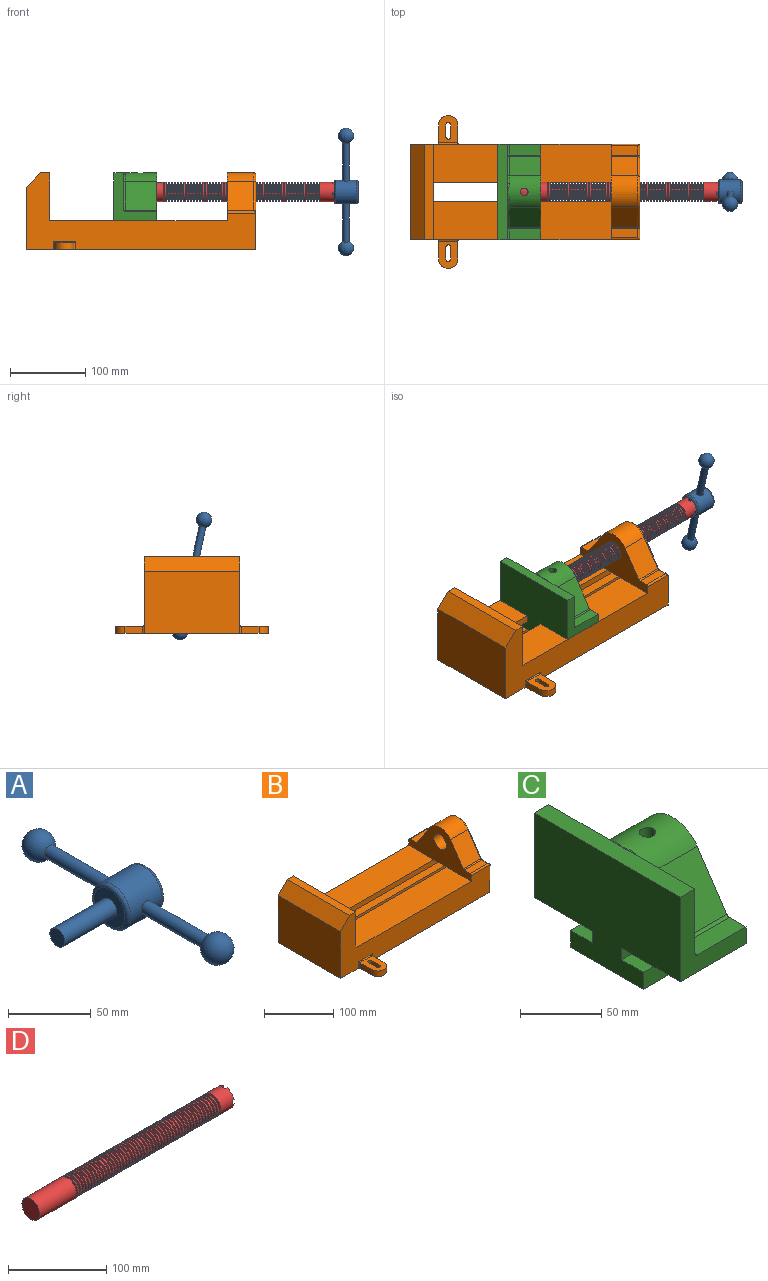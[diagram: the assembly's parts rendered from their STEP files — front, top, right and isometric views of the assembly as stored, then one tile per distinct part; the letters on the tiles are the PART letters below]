
ASSEMBLY  parts=4 mates=4
PART A: 11 faces, bbox 76.2x172.7x34.4 mm
  f0: sphere r=10.16mm, area 1231.8mm2, adj f1
  f1: cylinder r=4.45mm len=51.82mm, axis (0,1,0), area 1438.5mm2, adj f0,f4
  f2: sphere r=10.16mm, area 1231.8mm2, adj f3
  f3: cylinder r=4.45mm len=51.82mm, axis (0,1,0), area 1438.5mm2, adj f2,f4
  f4: cylinder r=15.88mm len=31.75mm, axis (-1,0,0), area 2534.7mm2, adj f1,f3,f9,f10
  f5: cylinder r=6.35mm len=44.45mm, axis (-1,0,0), area 1773.5mm2, adj f6,f8
  f6: plane 12.7x12.7mm, normal (-1,0,0), area 126.7mm2, adj f5
  f7: plane 26.67x26.67mm, normal (1,0,0), area 558.6mm2, adj f10
  f8: plane 26.67x26.67mm, normal (-1,0,0), area 432mm2, adj f5,f9
  f9: torus R=13.33mm, axis (1,0,0), area 374.8mm2, adj f4,f8
  f10: torus R=13.33mm, axis (1,0,0), area 374.8mm2, adj f4,f7
PART B: 61 faces, bbox 304.8x203.2x103.7 mm
  f0: plane 304.8x101.6mm, normal (0,1,0), area 13520.3mm2, adj f3,f4,f5,f6,f7,f8,f9,f16
  f1: plane 304.8x101.6mm, normal (0,-1,0), area 13520.3mm2, adj f2,f3,f5,f6,f7,f8,f9,f16
  f2: plane 234.95x50.8mm, normal (0,0,1), area 11935.5mm2, adj f1,f5,f16,f26
  f3: plane 127x99.06mm, normal (1,0,0), area 7097.5mm2, adj f0,f1,f9,f14,f17,f18,f19,f20
  f4: plane 234.95x50.8mm, normal (0,0,1), area 11935.5mm2, adj f0,f5,f16,f27
  f5: plane 127x101.6mm, normal (1,0,0), area 9516.1mm2, adj f0,f1,f2,f4,f6,f9,f18,f19
  f6: plane 127x12.7mm, normal (0,0,1), area 1612.9mm2, adj f0,f1,f5,f7
  f7: plane 127x19.05mm, normal (-0.71,0,0.71), area 3421.5mm2, adj f0,f1,f6,f8
  f8: plane 127x82.55mm, normal (-1,0,0), area 10483.8mm2, adj f0,f1,f7,f9
  f9: plane 304.8x203.2mm, normal (0,0,-1), area 33298.3mm2, adj f0,f1,f3,f5,f8,f21,f22,f39
  f10: plane 35.56x11.98mm, normal (0,0,1), area 426mm2, adj f16,f28,f29,f30
  f11: plane 38.43x35.56mm, normal (0,0.83,0.56), area 1645.4mm2, adj f12,f16,f29,f32
  f12: cylinder r=25.4mm len=42.19mm, axis (1,0,0), area 1770.2mm2, adj f11,f13,f16,f33
  f13: plane 38.43x35.56mm, normal (0,-0.83,0.56), area 1645.4mm2, adj f12,f16,f34,f35
  f14: cylinder r=12.7mm len=38.1mm, axis (1,0,0), area 3040.2mm2, adj f3,f16
  f15: plane 35.56x11.98mm, normal (0,0,1), area 426mm2, adj f16,f34,f36,f38
  f16: plane 127x63.5mm, normal (-1,0,0), area 4155.5mm2, adj f0,f1,f2,f4,f10,f11,f12,f13
  f17: plane 38.1x25.4mm, normal (0,0,-1), area 967.7mm2, adj f3,f16,f26,f27
  f18: plane 273.05x19.05mm, normal (0,0,-1), area 5201.6mm2, adj f3,f5,f19,f26
  f19: plane 273.05x12.7mm, normal (0,1,0), area 3467.7mm2, adj f3,f5,f18,f20
  f20: plane 273.05x19.05mm, normal (0,0,1), area 5201.6mm2, adj f3,f5,f19,f21
  f21: plane 273.05x16.51mm, normal (0,1,0), area 4508.1mm2, adj f3,f5,f9,f20
  f22: plane 273.05x16.51mm, normal (0,-1,0), area 4508.1mm2, adj f3,f5,f9,f23
  f23: plane 273.05x19.05mm, normal (0,0,1), area 5201.6mm2, adj f3,f5,f22,f24
  f24: plane 273.05x12.7mm, normal (0,-1,0), area 3467.7mm2, adj f3,f5,f23,f25
  f25: plane 273.05x19.05mm, normal (0,0,-1), area 5201.6mm2, adj f3,f5,f24,f27
  f26: plane 273.05x8.89mm, normal (0,1,0), area 2427.4mm2, adj f2,f3,f5,f17,f18
  f27: plane 273.05x8.89mm, normal (0,-1,0), area 2427.4mm2, adj f3,f4,f5,f17,f25
  f28: cylinder r=2.54mm len=38.1mm, axis (1,0,0), area 148.3mm2, adj f0,f10,f16,f30
  f29: cylinder r=2.54mm len=35.56mm, axis (-1,0,0), area 88.5mm2, adj f10,f11,f16,f31
  f30: cylinder r=2.54mm len=14.52mm, axis (0,1,0), area 54.3mm2, adj f3,f10,f28,f31
  f31: torus R=5.08mm, axis (-1,0,0), area 13.5mm2, adj f3,f29,f30,f32
  f32: cylinder r=2.54mm len=39.84mm, axis (0,0.56,-0.83), area 184.6mm2, adj f3,f11,f31,f33
  f33: torus R=22.86mm, axis (-1,0,0), area 191.4mm2, adj f3,f12,f32,f35
  f34: cylinder r=2.54mm len=35.56mm, axis (-1,0,0), area 88.5mm2, adj f13,f15,f16,f37
  f35: cylinder r=2.54mm len=39.84mm, axis (0,0.56,0.83), area 184.6mm2, adj f3,f13,f33,f37
  f36: cylinder r=2.54mm len=38.1mm, axis (-1,0,0), area 148.3mm2, adj f1,f15,f16,f38
  f37: torus R=5.08mm, axis (-1,0,0), area 13.5mm2, adj f3,f34,f35,f38
  f38: cylinder r=2.54mm len=14.52mm, axis (0,1,0), area 54.3mm2, adj f3,f15,f36,f37
  f39: plane 23.88x9.53mm, normal (-1,0,0), area 227.4mm2, adj f9,f45,f46,f60
  f40: plane 23.88x9.53mm, normal (1,0,0), area 227.4mm2, adj f9,f45,f46,f58
  f41: cylinder r=3.3mm len=9.53mm, axis (0,0,-1), area 98.8mm2, adj f9,f42,f44,f46
  f42: plane 15.62x9.53mm, normal (-1,0,0), area 148.8mm2, adj f9,f41,f43,f46
  f43: cylinder r=3.3mm len=9.53mm, axis (0,0,-1), area 98.8mm2, adj f9,f42,f44,f46
  f44: plane 15.62x9.53mm, normal (1,0,0), area 148.8mm2, adj f9,f41,f43,f46
  f45: cylinder r=12.7mm len=25.4mm, axis (0,0,-1), area 380mm2, adj f9,f39,f40,f46
  f46: plane 36.58x25.4mm, normal (0,0,1), area 722.4mm2, adj f39,f40,f41,f42,f43,f44,f45,f59
  f47: plane 23.88x9.53mm, normal (-1,0,0), area 227.4mm2, adj f9,f53,f54,f56
  f48: plane 23.88x9.53mm, normal (1,0,0), area 227.4mm2, adj f9,f53,f54,f55
  f49: cylinder r=3.3mm len=9.53mm, axis (0,0,-1), area 98.8mm2, adj f9,f50,f52,f54
  f50: plane 15.62x9.53mm, normal (-1,0,0), area 148.8mm2, adj f9,f49,f51,f54
  f51: cylinder r=3.3mm len=9.53mm, axis (0,0,-1), area 98.8mm2, adj f9,f50,f52,f54
  f52: plane 15.62x9.53mm, normal (1,0,0), area 148.8mm2, adj f9,f49,f51,f54
  f53: cylinder r=12.7mm len=25.4mm, axis (0,0,-1), area 380mm2, adj f9,f47,f48,f54
  f54: plane 36.58x25.4mm, normal (0,0,1), area 722.4mm2, adj f47,f48,f49,f50,f51,f52,f53,f57
  f55: cylinder r=1.52mm len=11.05mm, axis (0,0,-1), area 24.1mm2, adj f0,f9,f48,f57
  f56: cylinder r=1.52mm len=11.05mm, axis (0,0,1), area 24.1mm2, adj f0,f9,f47,f57
  f57: cylinder r=1.52mm len=28.45mm, axis (1,0,0), area 63.5mm2, adj f0,f54,f55,f56
  f58: cylinder r=1.52mm len=11.05mm, axis (0,0,1), area 24.1mm2, adj f1,f9,f40,f59
  f59: cylinder r=1.52mm len=28.45mm, axis (-1,0,0), area 63.5mm2, adj f1,f46,f58,f60
  f60: cylinder r=1.52mm len=11.05mm, axis (0,0,-1), area 24.1mm2, adj f1,f9,f39,f59
PART C: 36 faces, bbox 57.2x127x89 mm
  f0: plane 57.15x50.8mm, normal (0,0,-1), area 2903.2mm2, adj f6,f9,f10,f23
  f1: cylinder r=12.7mm len=44.45mm, axis (1,0,0), area 3464.3mm2, adj f6,f15,f16
  f2: plane 41.91x14.52mm, normal (0,0,1), area 608.5mm2, adj f6,f11,f24,f25
  f3: plane 51.86x48.26mm, normal (1,0,0), area 1495.7mm2, adj f8,f10,f31,f33,f35
  f4: plane 51.86x48.26mm, normal (1,0,0), area 1495.7mm2, adj f8,f11,f24,f28,f29
  f5: plane 57.15x50.8mm, normal (0,0,-1), area 2903.2mm2, adj f6,f9,f11,f22
  f6: plane 127x85.09mm, normal (1,0,0), area 5190.6mm2, adj f0,f1,f2,f5,f7,f10,f11,f12
  f7: plane 41.91x14.52mm, normal (0,0,1), area 608.5mm2, adj f6,f10,f30,f31
  f8: plane 127x12.7mm, normal (0,0,1), area 1612.9mm2, adj f3,f4,f9,f10,f11,f26,f34
  f9: plane 127x85.09mm, normal (-1,0,0), area 9096.8mm2, adj f0,f5,f8,f10,f11,f17,f18,f19
  f10: plane 63.5x57.15mm, normal (0,-1,0), area 1372.3mm2, adj f0,f3,f6,f7,f8,f9,f31
  f11: plane 63.5x57.15mm, normal (0,1,0), area 1372.3mm2, adj f2,f4,f5,f6,f8,f9,f24
  f12: plane 41.91x38.43mm, normal (0,-0.83,0.56), area 1939.2mm2, adj f6,f13,f30,f33
  f13: cylinder r=25.4mm len=44.45mm, axis (1,0,0), area 2026.5mm2, adj f6,f12,f14,f16,f26,f28,f34,f35
  f14: plane 41.91x38.43mm, normal (0,0.83,0.56), area 1939.2mm2, adj f6,f13,f25,f29
  f15: plane 25.4x25.4mm, normal (1,0,0), area 506.7mm2, adj f1
  f16: cylinder r=5.08mm len=13.76mm, axis (0,0,1), area 414mm2, adj f1,f13
  f17: plane 57.15x19.05mm, normal (0,0,1), area 1088.7mm2, adj f6,f9,f18,f23
  f18: plane 57.15x12.7mm, normal (0,-1,0), area 725.8mm2, adj f6,f9,f17,f19
  f19: plane 63.5x57.15mm, normal (0,0,-1), area 3629mm2, adj f6,f9,f18,f20
  f20: plane 57.15x12.7mm, normal (0,1,0), area 725.8mm2, adj f6,f9,f19,f21
  f21: plane 57.15x19.05mm, normal (0,0,1), area 1088.7mm2, adj f6,f9,f20,f22
  f22: plane 57.15x8.89mm, normal (0,1,0), area 508.1mm2, adj f5,f6,f9,f21
  f23: plane 57.15x8.89mm, normal (0,-1,0), area 508.1mm2, adj f0,f6,f9,f17
  f24: cylinder r=2.54mm len=14.52mm, axis (0,-1,0), area 57.9mm2, adj f2,f4,f11,f27
  f25: cylinder r=2.54mm len=41.91mm, axis (1,0,0), area 104.3mm2, adj f2,f6,f14,f27
  f26: bspline ~12.24x2.8mm, area 20.9mm2, adj f8,f13,f28
  f27: sphere r=2.54mm, area 6.3mm2, adj f24,f25,f29
  f28: torus R=27.94mm, axis (1,0,0), area 57.8mm2, adj f4,f13,f26,f29
  f29: cylinder r=2.54mm len=39.84mm, axis (0,-0.56,0.83), area 184.6mm2, adj f4,f14,f27,f28
  f30: cylinder r=2.54mm len=41.91mm, axis (1,0,0), area 104.3mm2, adj f6,f7,f12,f32
  f31: cylinder r=2.54mm len=14.52mm, axis (0,-1,0), area 57.9mm2, adj f3,f7,f10,f32
  f32: sphere r=2.54mm, area 6.3mm2, adj f30,f31,f33
  f33: cylinder r=2.54mm len=39.84mm, axis (0,-0.56,-0.83), area 184.6mm2, adj f3,f12,f32,f35
  f34: bspline ~12.24x2.8mm, area 20.9mm2, adj f8,f13,f35
  f35: torus R=27.94mm, axis (1,0,0), area 57.8mm2, adj f3,f13,f33,f34
PART D: 220 faces, bbox 279.4x25.4x25.4 mm
  f0: cylinder r=12.7mm len=25.4mm, axis (-1,0,0), area 1468.2mm2, adj f1,f2,f3,f5,f7,f208,f209,f210
  f1: plane 9.9x9.9mm, normal (1,0,0), area 62.3mm2, adj f0,f4,f213,f216
  f2: plane 9.9x9.9mm, normal (1,0,0), area 62.3mm2, adj f0,f4,f210,f218
  f3: plane 9.9x9.9mm, normal (1,0,0), area 62.3mm2, adj f0,f4,f209,f212
  f4: cylinder r=6.35mm len=25.4mm, axis (1,0,0), area 960.3mm2, adj f1,f2,f3,f5,f6,f208,f209,f210
  f5: plane 9.9x9.9mm, normal (1,0,0), area 62.3mm2, adj f0,f4,f215,f217
  f6: plane 12.7x12.7mm, normal (1,0,0), area 126.7mm2, adj f4
  f7: cone r=12.7mm half-angle=76deg, axis (1,0,0), area 188mm2, adj f0,f9
  f8: cone r=10.16mm half-angle=76deg, axis (-1,0,0), area 188mm2, adj f9,f10
  f9: cylinder r=10.16mm len=20.32mm, axis (1,0,0), area 81.1mm2, adj f7,f8
  f10: cylinder r=12.7mm len=25.4mm, axis (-1,0,0), area 131.7mm2, adj f8,f11
  f11: cone r=12.7mm half-angle=76deg, axis (1,0,0), area 188mm2, adj f10,f13
  f12: cone r=10.16mm half-angle=76deg, axis (-1,0,0), area 188mm2, adj f13,f14
  f13: cylinder r=10.16mm len=20.32mm, axis (1,0,0), area 81.1mm2, adj f11,f12
  f14: cylinder r=12.7mm len=25.4mm, axis (-1,0,0), area 131.7mm2, adj f12,f15
  f15: cone r=12.7mm half-angle=76deg, axis (1,0,0), area 188mm2, adj f14,f17
  f16: cone r=10.16mm half-angle=76deg, axis (-1,0,0), area 188mm2, adj f17,f18
  f17: cylinder r=10.16mm len=20.32mm, axis (1,0,0), area 81.1mm2, adj f15,f16
  f18: cylinder r=12.7mm len=25.4mm, axis (-1,0,0), area 131.7mm2, adj f16,f19
  f19: cone r=12.7mm half-angle=76deg, axis (1,0,0), area 188mm2, adj f18,f21
  f20: cone r=10.16mm half-angle=76deg, axis (-1,0,0), area 188mm2, adj f21,f22
  f21: cylinder r=10.16mm len=20.32mm, axis (1,0,0), area 81.1mm2, adj f19,f20
  f22: cylinder r=12.7mm len=25.4mm, axis (-1,0,0), area 131.7mm2, adj f20,f23
  f23: cone r=12.7mm half-angle=76deg, axis (1,0,0), area 188mm2, adj f22,f25
  f24: cone r=10.16mm half-angle=76deg, axis (-1,0,0), area 188mm2, adj f25,f26
  f25: cylinder r=10.16mm len=20.32mm, axis (1,0,0), area 81.1mm2, adj f23,f24
  f26: cylinder r=12.7mm len=25.4mm, axis (-1,0,0), area 131.7mm2, adj f24,f27
  f27: cone r=12.7mm half-angle=76deg, axis (1,0,0), area 188mm2, adj f26,f29
  f28: cone r=10.16mm half-angle=76deg, axis (-1,0,0), area 188mm2, adj f29,f30
  f29: cylinder r=10.16mm len=20.32mm, axis (1,0,0), area 81.1mm2, adj f27,f28
  f30: cylinder r=12.7mm len=25.4mm, axis (-1,0,0), area 131.7mm2, adj f28,f31
  f31: cone r=12.7mm half-angle=76deg, axis (1,0,0), area 188mm2, adj f30,f33
  f32: cone r=10.16mm half-angle=76deg, axis (-1,0,0), area 188mm2, adj f33,f34
  f33: cylinder r=10.16mm len=20.32mm, axis (1,0,0), area 81.1mm2, adj f31,f32
  f34: cylinder r=12.7mm len=25.4mm, axis (-1,0,0), area 131.7mm2, adj f32,f35
  f35: cone r=12.7mm half-angle=76deg, axis (1,0,0), area 188mm2, adj f34,f37
  f36: cone r=10.16mm half-angle=76deg, axis (-1,0,0), area 188mm2, adj f37,f38
  f37: cylinder r=10.16mm len=20.32mm, axis (1,0,0), area 81.1mm2, adj f35,f36
  f38: cylinder r=12.7mm len=25.4mm, axis (-1,0,0), area 131.7mm2, adj f36,f39
  f39: cone r=12.7mm half-angle=76deg, axis (1,0,0), area 188mm2, adj f38,f41
  f40: cone r=10.16mm half-angle=76deg, axis (-1,0,0), area 188mm2, adj f41,f42
  f41: cylinder r=10.16mm len=20.32mm, axis (1,0,0), area 81.1mm2, adj f39,f40
  f42: cylinder r=12.7mm len=25.4mm, axis (-1,0,0), area 131.7mm2, adj f40,f43
  f43: cone r=12.7mm half-angle=76deg, axis (1,0,0), area 188mm2, adj f42,f45
  f44: cone r=10.16mm half-angle=76deg, axis (-1,0,0), area 188mm2, adj f45,f46
  f45: cylinder r=10.16mm len=20.32mm, axis (1,0,0), area 81.1mm2, adj f43,f44
  f46: cylinder r=12.7mm len=25.4mm, axis (-1,0,0), area 131.7mm2, adj f44,f47
  f47: cone r=12.7mm half-angle=76deg, axis (1,0,0), area 188mm2, adj f46,f49
  f48: cone r=10.16mm half-angle=76deg, axis (-1,0,0), area 188mm2, adj f49,f50
  f49: cylinder r=10.16mm len=20.32mm, axis (1,0,0), area 81.1mm2, adj f47,f48
  f50: cylinder r=12.7mm len=25.4mm, axis (-1,0,0), area 131.7mm2, adj f48,f51
  f51: cone r=12.7mm half-angle=76deg, axis (1,0,0), area 188mm2, adj f50,f53
  f52: cone r=10.16mm half-angle=76deg, axis (-1,0,0), area 188mm2, adj f53,f54
  f53: cylinder r=10.16mm len=20.32mm, axis (1,0,0), area 81.1mm2, adj f51,f52
  f54: cylinder r=12.7mm len=25.4mm, axis (-1,0,0), area 131.7mm2, adj f52,f55
  f55: cone r=12.7mm half-angle=76deg, axis (1,0,0), area 188mm2, adj f54,f57
  f56: cone r=10.16mm half-angle=76deg, axis (-1,0,0), area 188mm2, adj f57,f58
  f57: cylinder r=10.16mm len=20.32mm, axis (1,0,0), area 81.1mm2, adj f55,f56
  f58: cylinder r=12.7mm len=25.4mm, axis (-1,0,0), area 131.7mm2, adj f56,f59
  f59: cone r=12.7mm half-angle=76deg, axis (1,0,0), area 188mm2, adj f58,f61
  f60: cone r=10.16mm half-angle=76deg, axis (-1,0,0), area 188mm2, adj f61,f62
  f61: cylinder r=10.16mm len=20.32mm, axis (1,0,0), area 81.1mm2, adj f59,f60
  f62: cylinder r=12.7mm len=25.4mm, axis (-1,0,0), area 131.7mm2, adj f60,f63
  f63: cone r=12.7mm half-angle=76deg, axis (1,0,0), area 188mm2, adj f62,f65
  f64: cone r=10.16mm half-angle=76deg, axis (-1,0,0), area 188mm2, adj f65,f66
  f65: cylinder r=10.16mm len=20.32mm, axis (1,0,0), area 81.1mm2, adj f63,f64
  f66: cylinder r=12.7mm len=25.4mm, axis (-1,0,0), area 131.7mm2, adj f64,f67
  f67: cone r=12.7mm half-angle=76deg, axis (1,0,0), area 188mm2, adj f66,f69
  f68: cone r=10.16mm half-angle=76deg, axis (-1,0,0), area 188mm2, adj f69,f70
  f69: cylinder r=10.16mm len=20.32mm, axis (1,0,0), area 81.1mm2, adj f67,f68
  f70: cylinder r=12.7mm len=25.4mm, axis (-1,0,0), area 131.7mm2, adj f68,f71
  f71: cone r=12.7mm half-angle=76deg, axis (1,0,0), area 188mm2, adj f70,f73
  f72: cone r=10.16mm half-angle=76deg, axis (-1,0,0), area 188mm2, adj f73,f74
  f73: cylinder r=10.16mm len=20.32mm, axis (1,0,0), area 81.1mm2, adj f71,f72
  f74: cylinder r=12.7mm len=25.4mm, axis (-1,0,0), area 131.7mm2, adj f72,f75
  f75: cone r=12.7mm half-angle=76deg, axis (1,0,0), area 188mm2, adj f74,f77
  f76: cone r=10.16mm half-angle=76deg, axis (-1,0,0), area 188mm2, adj f77,f78
  f77: cylinder r=10.16mm len=20.32mm, axis (1,0,0), area 81.1mm2, adj f75,f76
  f78: cylinder r=12.7mm len=25.4mm, axis (-1,0,0), area 131.7mm2, adj f76,f79
  f79: cone r=12.7mm half-angle=76deg, axis (1,0,0), area 188mm2, adj f78,f81
  f80: cone r=10.16mm half-angle=76deg, axis (-1,0,0), area 188mm2, adj f81,f82
  f81: cylinder r=10.16mm len=20.32mm, axis (1,0,0), area 81.1mm2, adj f79,f80
  f82: cylinder r=12.7mm len=25.4mm, axis (-1,0,0), area 131.7mm2, adj f80,f83
  f83: cone r=12.7mm half-angle=76deg, axis (1,0,0), area 188mm2, adj f82,f85
  f84: cone r=10.16mm half-angle=76deg, axis (-1,0,0), area 188mm2, adj f85,f86
  f85: cylinder r=10.16mm len=20.32mm, axis (1,0,0), area 81.1mm2, adj f83,f84
  f86: cylinder r=12.7mm len=25.4mm, axis (-1,0,0), area 131.7mm2, adj f84,f87
  f87: cone r=12.7mm half-angle=76deg, axis (1,0,0), area 188mm2, adj f86,f89
  f88: cone r=10.16mm half-angle=76deg, axis (-1,0,0), area 188mm2, adj f89,f90
  f89: cylinder r=10.16mm len=20.32mm, axis (1,0,0), area 81.1mm2, adj f87,f88
  f90: cylinder r=12.7mm len=25.4mm, axis (-1,0,0), area 131.7mm2, adj f88,f91
  f91: cone r=12.7mm half-angle=76deg, axis (1,0,0), area 188mm2, adj f90,f93
  f92: cone r=10.16mm half-angle=76deg, axis (-1,0,0), area 188mm2, adj f93,f94
  f93: cylinder r=10.16mm len=20.32mm, axis (1,0,0), area 81.1mm2, adj f91,f92
  f94: cylinder r=12.7mm len=25.4mm, axis (-1,0,0), area 131.7mm2, adj f92,f95
  f95: cone r=12.7mm half-angle=76deg, axis (1,0,0), area 188mm2, adj f94,f97
  f96: cone r=10.16mm half-angle=76deg, axis (-1,0,0), area 188mm2, adj f97,f98
  f97: cylinder r=10.16mm len=20.32mm, axis (1,0,0), area 81.1mm2, adj f95,f96
  f98: cylinder r=12.7mm len=25.4mm, axis (-1,0,0), area 131.7mm2, adj f96,f99
  f99: cone r=12.7mm half-angle=76deg, axis (1,0,0), area 188mm2, adj f98,f101
  f100: cone r=10.16mm half-angle=76deg, axis (-1,0,0), area 188mm2, adj f101,f102
  f101: cylinder r=10.16mm len=20.32mm, axis (1,0,0), area 81.1mm2, adj f99,f100
  f102: cylinder r=12.7mm len=25.4mm, axis (-1,0,0), area 131.7mm2, adj f100,f103
  f103: cone r=12.7mm half-angle=76deg, axis (1,0,0), area 188mm2, adj f102,f105
  f104: cone r=10.16mm half-angle=76deg, axis (-1,0,0), area 188mm2, adj f105,f106
  f105: cylinder r=10.16mm len=20.32mm, axis (1,0,0), area 81.1mm2, adj f103,f104
  f106: cylinder r=12.7mm len=25.4mm, axis (-1,0,0), area 131.7mm2, adj f104,f107
  f107: cone r=12.7mm half-angle=76deg, axis (1,0,0), area 188mm2, adj f106,f109
  f108: cone r=10.16mm half-angle=76deg, axis (-1,0,0), area 188mm2, adj f109,f110
  f109: cylinder r=10.16mm len=20.32mm, axis (1,0,0), area 81.1mm2, adj f107,f108
  f110: cylinder r=12.7mm len=25.4mm, axis (-1,0,0), area 131.7mm2, adj f108,f111
  f111: cone r=12.7mm half-angle=76deg, axis (1,0,0), area 188mm2, adj f110,f113
  f112: cone r=10.16mm half-angle=76deg, axis (-1,0,0), area 188mm2, adj f113,f114
  f113: cylinder r=10.16mm len=20.32mm, axis (1,0,0), area 81.1mm2, adj f111,f112
  f114: cylinder r=12.7mm len=25.4mm, axis (-1,0,0), area 131.7mm2, adj f112,f115
  f115: cone r=12.7mm half-angle=76deg, axis (1,0,0), area 188mm2, adj f114,f117
  f116: cone r=10.16mm half-angle=76deg, axis (-1,0,0), area 188mm2, adj f117,f118
  f117: cylinder r=10.16mm len=20.32mm, axis (1,0,0), area 81.1mm2, adj f115,f116
  f118: cylinder r=12.7mm len=25.4mm, axis (-1,0,0), area 131.7mm2, adj f116,f119
  f119: cone r=12.7mm half-angle=76deg, axis (1,0,0), area 188mm2, adj f118,f121
  f120: cone r=10.16mm half-angle=76deg, axis (-1,0,0), area 188mm2, adj f121,f122
  f121: cylinder r=10.16mm len=20.32mm, axis (1,0,0), area 81.1mm2, adj f119,f120
  f122: cylinder r=12.7mm len=25.4mm, axis (-1,0,0), area 131.7mm2, adj f120,f123
  f123: cone r=12.7mm half-angle=76deg, axis (1,0,0), area 188mm2, adj f122,f125
  f124: cone r=10.16mm half-angle=76deg, axis (-1,0,0), area 188mm2, adj f125,f126
  f125: cylinder r=10.16mm len=20.32mm, axis (1,0,0), area 81.1mm2, adj f123,f124
  f126: cylinder r=12.7mm len=25.4mm, axis (-1,0,0), area 131.7mm2, adj f124,f127
  f127: cone r=12.7mm half-angle=76deg, axis (1,0,0), area 188mm2, adj f126,f129
  f128: cone r=10.16mm half-angle=76deg, axis (-1,0,0), area 188mm2, adj f129,f130
  f129: cylinder r=10.16mm len=20.32mm, axis (1,0,0), area 81.1mm2, adj f127,f128
  f130: cylinder r=12.7mm len=25.4mm, axis (-1,0,0), area 131.7mm2, adj f128,f131
  f131: cone r=12.7mm half-angle=76deg, axis (1,0,0), area 188mm2, adj f130,f133
  f132: cone r=10.16mm half-angle=76deg, axis (-1,0,0), area 188mm2, adj f133,f134
  f133: cylinder r=10.16mm len=20.32mm, axis (1,0,0), area 81.1mm2, adj f131,f132
  f134: cylinder r=12.7mm len=25.4mm, axis (-1,0,0), area 131.7mm2, adj f132,f135
  f135: cone r=12.7mm half-angle=76deg, axis (1,0,0), area 188mm2, adj f134,f137
  f136: cone r=10.16mm half-angle=76deg, axis (-1,0,0), area 188mm2, adj f137,f138
  f137: cylinder r=10.16mm len=20.32mm, axis (1,0,0), area 81.1mm2, adj f135,f136
  f138: cylinder r=12.7mm len=25.4mm, axis (-1,0,0), area 131.7mm2, adj f136,f139
  f139: cone r=12.7mm half-angle=76deg, axis (1,0,0), area 188mm2, adj f138,f141
  f140: cone r=10.16mm half-angle=76deg, axis (-1,0,0), area 188mm2, adj f141,f142
  f141: cylinder r=10.16mm len=20.32mm, axis (1,0,0), area 81.1mm2, adj f139,f140
  f142: cylinder r=12.7mm len=25.4mm, axis (-1,0,0), area 131.7mm2, adj f140,f143
  f143: cone r=12.7mm half-angle=76deg, axis (1,0,0), area 188mm2, adj f142,f145
  f144: cone r=10.16mm half-angle=76deg, axis (-1,0,0), area 188mm2, adj f145,f146
  f145: cylinder r=10.16mm len=20.32mm, axis (1,0,0), area 81.1mm2, adj f143,f144
  f146: cylinder r=12.7mm len=25.4mm, axis (-1,0,0), area 131.7mm2, adj f144,f147
  f147: cone r=12.7mm half-angle=76deg, axis (1,0,0), area 188mm2, adj f146,f149
  f148: cone r=10.16mm half-angle=76deg, axis (-1,0,0), area 188mm2, adj f149,f150
  f149: cylinder r=10.16mm len=20.32mm, axis (1,0,0), area 81.1mm2, adj f147,f148
  f150: cylinder r=12.7mm len=25.4mm, axis (-1,0,0), area 131.7mm2, adj f148,f151
  f151: cone r=12.7mm half-angle=76deg, axis (1,0,0), area 188mm2, adj f150,f153
  f152: cone r=10.16mm half-angle=76deg, axis (-1,0,0), area 188mm2, adj f153,f154
  f153: cylinder r=10.16mm len=20.32mm, axis (1,0,0), area 81.1mm2, adj f151,f152
  f154: cylinder r=12.7mm len=25.4mm, axis (-1,0,0), area 131.7mm2, adj f152,f155
  f155: cone r=12.7mm half-angle=76deg, axis (1,0,0), area 188mm2, adj f154,f157
  f156: cone r=10.16mm half-angle=76deg, axis (-1,0,0), area 188mm2, adj f157,f158
  f157: cylinder r=10.16mm len=20.32mm, axis (1,0,0), area 81.1mm2, adj f155,f156
  f158: cylinder r=12.7mm len=25.4mm, axis (-1,0,0), area 131.7mm2, adj f156,f159
  f159: cone r=12.7mm half-angle=76deg, axis (1,0,0), area 188mm2, adj f158,f161
  f160: cone r=10.16mm half-angle=76deg, axis (-1,0,0), area 188mm2, adj f161,f162
  f161: cylinder r=10.16mm len=20.32mm, axis (1,0,0), area 81.1mm2, adj f159,f160
  f162: cylinder r=12.7mm len=25.4mm, axis (-1,0,0), area 131.7mm2, adj f160,f163
  f163: cone r=12.7mm half-angle=76deg, axis (1,0,0), area 188mm2, adj f162,f165
  f164: cone r=10.16mm half-angle=76deg, axis (-1,0,0), area 188mm2, adj f165,f166
  f165: cylinder r=10.16mm len=20.32mm, axis (1,0,0), area 81.1mm2, adj f163,f164
  f166: cylinder r=12.7mm len=25.4mm, axis (-1,0,0), area 131.7mm2, adj f164,f167
  f167: cone r=12.7mm half-angle=76deg, axis (1,0,0), area 188mm2, adj f166,f169
  f168: cone r=10.16mm half-angle=76deg, axis (-1,0,0), area 188mm2, adj f169,f170
  f169: cylinder r=10.16mm len=20.32mm, axis (1,0,0), area 81.1mm2, adj f167,f168
  f170: cylinder r=12.7mm len=25.4mm, axis (-1,0,0), area 131.7mm2, adj f168,f171
  f171: cone r=12.7mm half-angle=76deg, axis (1,0,0), area 188mm2, adj f170,f173
  f172: cone r=10.16mm half-angle=76deg, axis (-1,0,0), area 188mm2, adj f173,f174
  f173: cylinder r=10.16mm len=20.32mm, axis (1,0,0), area 81.1mm2, adj f171,f172
  f174: cylinder r=12.7mm len=25.4mm, axis (-1,0,0), area 131.7mm2, adj f172,f175
  f175: cone r=12.7mm half-angle=76deg, axis (1,0,0), area 188mm2, adj f174,f177
  f176: cone r=10.16mm half-angle=76deg, axis (-1,0,0), area 188mm2, adj f177,f178
  f177: cylinder r=10.16mm len=20.32mm, axis (1,0,0), area 81.1mm2, adj f175,f176
  f178: cylinder r=12.7mm len=25.4mm, axis (-1,0,0), area 131.7mm2, adj f176,f179
  f179: cone r=12.7mm half-angle=76deg, axis (1,0,0), area 188mm2, adj f178,f181
  f180: cone r=10.16mm half-angle=76deg, axis (-1,0,0), area 188mm2, adj f181,f182
  f181: cylinder r=10.16mm len=20.32mm, axis (1,0,0), area 81.1mm2, adj f179,f180
  f182: cylinder r=12.7mm len=25.4mm, axis (-1,0,0), area 131.7mm2, adj f180,f183
  f183: cone r=12.7mm half-angle=76deg, axis (1,0,0), area 188mm2, adj f182,f185
  f184: cone r=10.16mm half-angle=76deg, axis (-1,0,0), area 188mm2, adj f185,f186
  f185: cylinder r=10.16mm len=20.32mm, axis (1,0,0), area 81.1mm2, adj f183,f184
  f186: cylinder r=12.7mm len=25.4mm, axis (-1,0,0), area 131.7mm2, adj f184,f187
  f187: cone r=12.7mm half-angle=76deg, axis (1,0,0), area 188mm2, adj f186,f189
  f188: cone r=10.16mm half-angle=76deg, axis (-1,0,0), area 188mm2, adj f189,f190
  f189: cylinder r=10.16mm len=20.32mm, axis (1,0,0), area 81.1mm2, adj f187,f188
  f190: cylinder r=12.7mm len=25.4mm, axis (-1,0,0), area 131.7mm2, adj f188,f191
  f191: cone r=12.7mm half-angle=76deg, axis (1,0,0), area 188mm2, adj f190,f193
  f192: cone r=10.16mm half-angle=76deg, axis (-1,0,0), area 188mm2, adj f193,f194
  f193: cylinder r=10.16mm len=20.32mm, axis (1,0,0), area 81.1mm2, adj f191,f192
  f194: cylinder r=12.7mm len=25.4mm, axis (-1,0,0), area 131.7mm2, adj f192,f195
  f195: cone r=12.7mm half-angle=76deg, axis (1,0,0), area 188mm2, adj f194,f197
  f196: cone r=10.16mm half-angle=76deg, axis (-1,0,0), area 188mm2, adj f197,f198
  f197: cylinder r=10.16mm len=20.32mm, axis (1,0,0), area 81.1mm2, adj f195,f196
  f198: cylinder r=12.7mm len=25.4mm, axis (-1,0,0), area 131.7mm2, adj f196,f199
  f199: cone r=12.7mm half-angle=76deg, axis (1,0,0), area 188mm2, adj f198,f201
  f200: cone r=10.16mm half-angle=76deg, axis (-1,0,0), area 188mm2, adj f201,f202
  f201: cylinder r=10.16mm len=20.32mm, axis (1,0,0), area 81.1mm2, adj f199,f200
  f202: cylinder r=12.7mm len=25.4mm, axis (-1,0,0), area 131.7mm2, adj f200,f203
  f203: cone r=12.7mm half-angle=76deg, axis (1,0,0), area 188mm2, adj f202,f205
  f204: cone r=10.16mm half-angle=76deg, axis (-1,0,0), area 188mm2, adj f205,f207
  f205: cylinder r=10.16mm len=20.32mm, axis (1,0,0), area 81.1mm2, adj f203,f204
  f206: plane 25.4x25.4mm, normal (-1,0,0), area 506.7mm2, adj f207
  f207: cylinder r=12.7mm len=52.45mm, axis (-1,0,0), area 4185.4mm2, adj f204,f206
  f208: plane 6.88x5.08mm, normal (1,0,0), area 32.7mm2, adj f0,f4,f209,f210
  f209: plane 6.62x2.54mm, normal (0,-1,0), area 16.8mm2, adj f0,f3,f4,f208
  f210: plane 6.62x2.54mm, normal (0,1,0), area 16.8mm2, adj f0,f2,f4,f208
  f211: plane 6.88x5.08mm, normal (1,0,0), area 32.7mm2, adj f0,f4,f212,f213
  f212: plane 6.62x2.54mm, normal (0,0,1), area 16.8mm2, adj f0,f3,f4,f211
  f213: plane 6.62x2.54mm, normal (0,0,-1), area 16.8mm2, adj f0,f1,f4,f211
  f214: plane 6.88x5.08mm, normal (1,0,0), area 32.7mm2, adj f0,f4,f215,f216
  f215: plane 6.62x2.54mm, normal (0,1,0), area 16.8mm2, adj f0,f4,f5,f214
  f216: plane 6.62x2.54mm, normal (0,-1,0), area 16.8mm2, adj f0,f1,f4,f214
  f217: plane 6.62x2.54mm, normal (0,0,-1), area 16.8mm2, adj f0,f4,f5,f219
  f218: plane 6.62x2.54mm, normal (0,0,1), area 16.8mm2, adj f0,f2,f4,f219
  f219: plane 6.88x5.08mm, normal (1,0,0), area 32.7mm2, adj f0,f4,f217,f218
PLACE A rot(axis=(-1,0,0),77.9deg) t=(65.81,-74.51,60.26)mm
PLACE B at identity fixed
PLACE C t=(84.86,0,0)mm
PLACE D rot(axis=(-1,0,0),77.9deg) t=(84.86,-74.51,60.26)mm
MATE fastened A.f5 <-> D.f4  axis (-1,0,0) through (103.91,0,76.2)mm
MATE revolute D.f7 <-> C.f28  axis (-1,0,0) through (-175.49,0,76.2)mm
MATE slider C.f9 <-> B.f5  axis (-1,0,0) through (-188.19,-63.5,38.1)mm
MATE cylindrical B.f12 <-> D.f7  axis (1,0,0) through (-19.05,0,76.2)mm
